# Revit family: CENTUM Gleitunterlage mit Abhebesicherung XL 80 stehend
name_source: partatom
category: HLS-Bauteile
revit_build: Autodesk Revit 2017 (Build: 20190508_0315(x64)
units: mm (PartAtom-declared; Revit-internal decimal feet)

## family parameters
Arbeitsebenenbasiert = Ja
Beim Laden mit Abzugskörper schneiden = Nein
Bemaßung runder Anschluss = Durchmesser verwenden
Gemeinsam genutzt = Ja
Immer vertikal = Nein
Raumberechnungspunkt = Nein
Teiletyp = Normal

## types (1)
- CENTUM Gleitunterlage mit Abhebesicherung XL 80 stehend
    Abhebesicherung = mit Abhebesicherung
    Artikelnummer = 1650801020
    Ausrichtung = stehend
    Breite Gleitstreifen = 40 mm  [stored 0.131234 ft]
    Breite Gleitunterlage = 115 mm
    C = 17 mm
    Fabrikat = MEFA
    Firma = MEFA Befestigungs- und Montagesysteme GmbH
    Gewicht = 0.00 kg
    Gewicht pro Bauteil = 0.00 kg
    Gleitreibungsfaktor = 0,15
    Haftreibungsfaktor = 0,2
    Höhe = 110 mm
    Höhe Gleitunterlage = 74 mm
    Langloch = 14x40 mm
    Länge Gleitstreifen = 60 mm  [stored 0.19685 ft]
    Länge Gleitunterlage = 70 mm  [stored 0.229659 ft]
    Sicherheitsfaktor = 1.54
    Stärke = 16 mm  [stored 0.0524934 ft]
    Vorgabe-Ansicht = 1219 mm
    max. Stärke Gleitplatte = 16 mm  [stored 0.0524934 ft]
    max. Temperaturbeständigkeit = 80 °C
    max. zul. Last (Paar) = 40 kN

note: [stored X ft] marks values corroborated as IEEE doubles in the binary element streams (Revit-internal decimal feet)

## geometry (parser evidence)
native form markers: Sweep x3
no freeform markers — native parametric forms only
